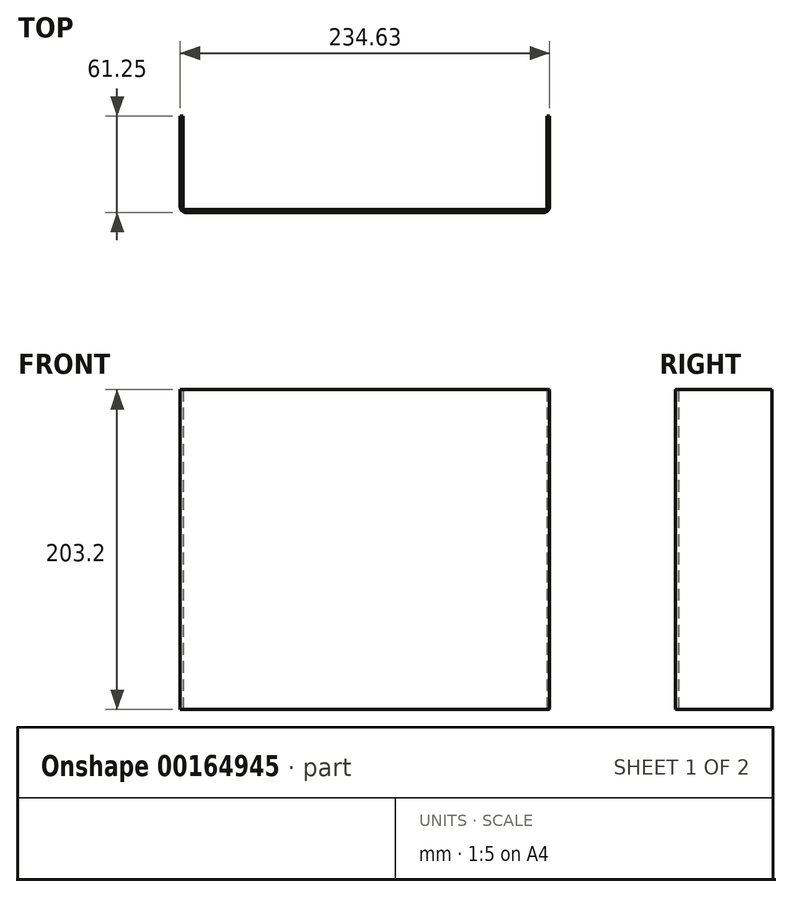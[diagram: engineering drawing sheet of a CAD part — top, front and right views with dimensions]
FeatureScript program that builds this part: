
annotation { "Feature Type Name" : "Feature", "Feature Type Description" : "" }
export const myFeature = defineFeature(function(context is Context, id is Id, definition is map)
    precondition{}
    {
        {
            var Q0;
            Q0=qCreatedBy(makeId("Top.planeOp"),FACE);
            var sketch = newSketch(context, id + "F0", { "sketchPlane" : qUnion([Q0])});
            skLineSegment(sketch, "E0", {"start": v(0, 0) * mm, "end": v(-1.7, 0) * mm});
            skLineSegment(sketch, "E1", {"start": v(0, 0) * mm, "end": v(0, -59.54) * mm});
            skLineSegment(sketch, "E2", {"start": v(0, -59.54) * mm, "end": v(231.21, -59.54) * mm});
            skLineSegment(sketch, "E3", {"start": v(232.92, -61.25) * mm, "end": v(-1.7, -61.25) * mm});
            skLineSegment(sketch, "E4", {"start": v(-1.7, -61.25) * mm, "end": v(-1.7, 0) * mm});
            skLineSegment(sketch, "E5", {"start": v(0, -59.54) * mm, "end": v(-1.7, -59.54) * mm, "construction": true});
            skLineSegment(sketch, "E6", {"start": v(115.6, -61.25) * mm, "end": v(115.6, -59.54) * mm, "construction": true});
            skLineSegment(sketch, "E7", {"start": v(231.21, -59.54) * mm, "end": v(231.21, 0) * mm});
            skLineSegment(sketch, "E8", {"start": v(231.21, 0) * mm, "end": v(232.92, 0) * mm});
            skLineSegment(sketch, "E9", {"start": v(232.92, 0) * mm, "end": v(232.92, -61.25) * mm});
            skSolve(sketch);
        }
        {
            var Q0;
            Q0=qSketchRegion(id+"F0",true);
            extrude(context, id + "F1", {"entities" : qUnion([Q0]), "depth" : 203.2 * mm});
        }
        {
            var Q0;
            Q0=makeQuery(id+"F1.opExtrude","SWEPT_EDGE",EDGE,{"disambiguationData":[OSD([sQuery(id+"F0.wireOp",EDGE,"E3"),sQuery(id+"F0.wireOp",EDGE,"E9")])]});
            var Q1;
            Q1=makeQuery(id+"F1.opExtrude","SWEPT_EDGE",EDGE,{"disambiguationData":[OSD([sQuery(id+"F0.wireOp",EDGE,"E3"),sQuery(id+"F0.wireOp",EDGE,"E4")])]});
            fillet(context, id + "F2", {"entities" : qUnion([Q0, Q1]), "radius" : 3.7 * mm, "tangentPropagation" : true, "allowEdgeOverflow" : false});
        }
        {
            var Q0;
            Q0=makeQuery(id+"F1.opExtrude","SWEPT_EDGE",EDGE,{"disambiguationData":[OSD([sQuery(id+"F0.wireOp",EDGE,"E1"),sQuery(id+"F0.wireOp",EDGE,"E2")])]});
            var Q1;
            Q1=makeQuery(id+"F1.opExtrude","SWEPT_EDGE",EDGE,{"disambiguationData":[OSD([sQuery(id+"F0.wireOp",EDGE,"E2"),sQuery(id+"F0.wireOp",EDGE,"E7")])]});
            fillet(context, id + "F3", {"entities" : qUnion([Q0, Q1]), "radius" : 1.98 * mm, "tangentPropagation" : true, "allowEdgeOverflow" : false});
        }
    });
